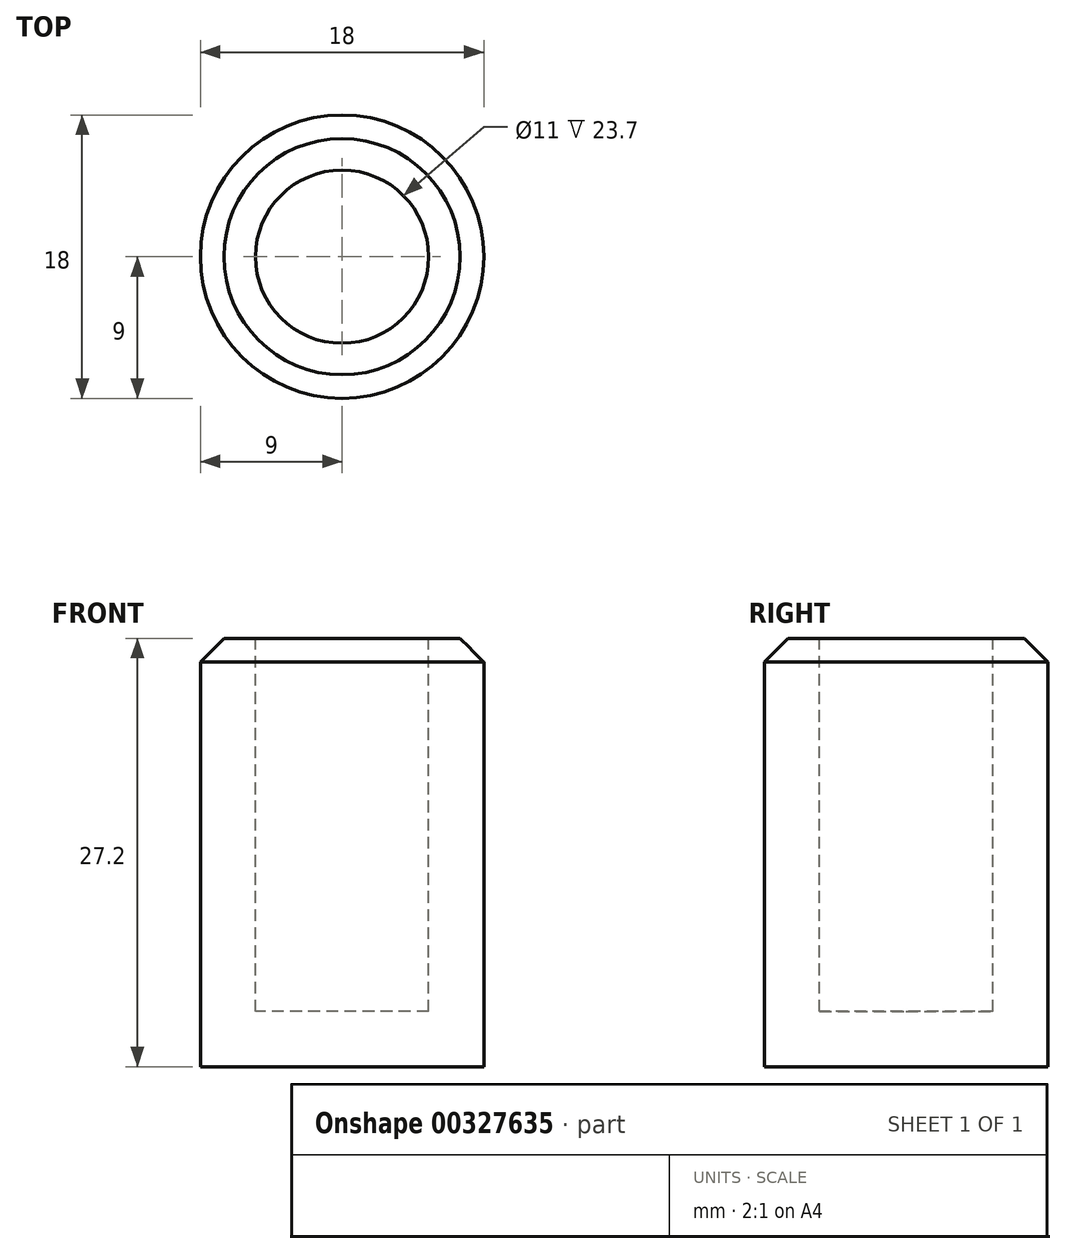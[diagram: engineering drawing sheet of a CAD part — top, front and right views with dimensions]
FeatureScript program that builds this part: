
annotation { "Feature Type Name" : "Feature", "Feature Type Description" : "" }
export const myFeature = defineFeature(function(context is Context, id is Id, definition is map)
    precondition{}
    {
        {
            var Q0;
            Q0=qCreatedBy(makeId("Top.planeOp"),FACE);
            var sketch = newSketch(context, id + "F0", { "sketchPlane" : qUnion([Q0])});
            skCircle(sketch, "E0", {"center": v(0, 0) * mm, "radius": 9 * mm});
            skSolve(sketch);
        }
        {
            var Q0;
            Q0 = qSketchRegion(id + "F0", true);
            extrude(context, id + "F1", {"entities" : qUnion([Q0]), "oppositeDirection" : true, "depth" : 27.2 * mm});
        }
        {
            var Q0;
            Q0=makeQuery(id+"F1.opExtrude","CAP_FACE",FACE,{"disambiguationData":[OSD([sQuery(id+"F0.wireOp",EDGE,"E0")])],"isStart":true});
            var sketch = newSketch(context, id + "F2", { "sketchPlane" : qUnion([Q0])});
            skCircle(sketch, "E1", {"center": v(0, 0) * mm, "radius": 5.5 * mm});
            skSolve(sketch);
        }
        {
            var Q0;
            Q0 = qSketchRegion(id + "F2", true);
            extrude(context, id + "F3", {"entities" : qUnion([Q0]), "operationType" : NewBodyOperationType.REMOVE, "oppositeDirection" : true, "depth" : 23.7 * mm});
        }
        {
            var Q0;
            Q0=makeQuery(id+"F1.opExtrude","CAP_EDGE",EDGE,{"disambiguationData":[OSD([sQuery(id+"F0.wireOp",EDGE,"E0")])],"isStart":true});
            chamfer(context, id + "F4", {"entities" : qUnion([Q0]), "width" : 1.5 * mm, "tangentPropagation" : true});
        }
    });
